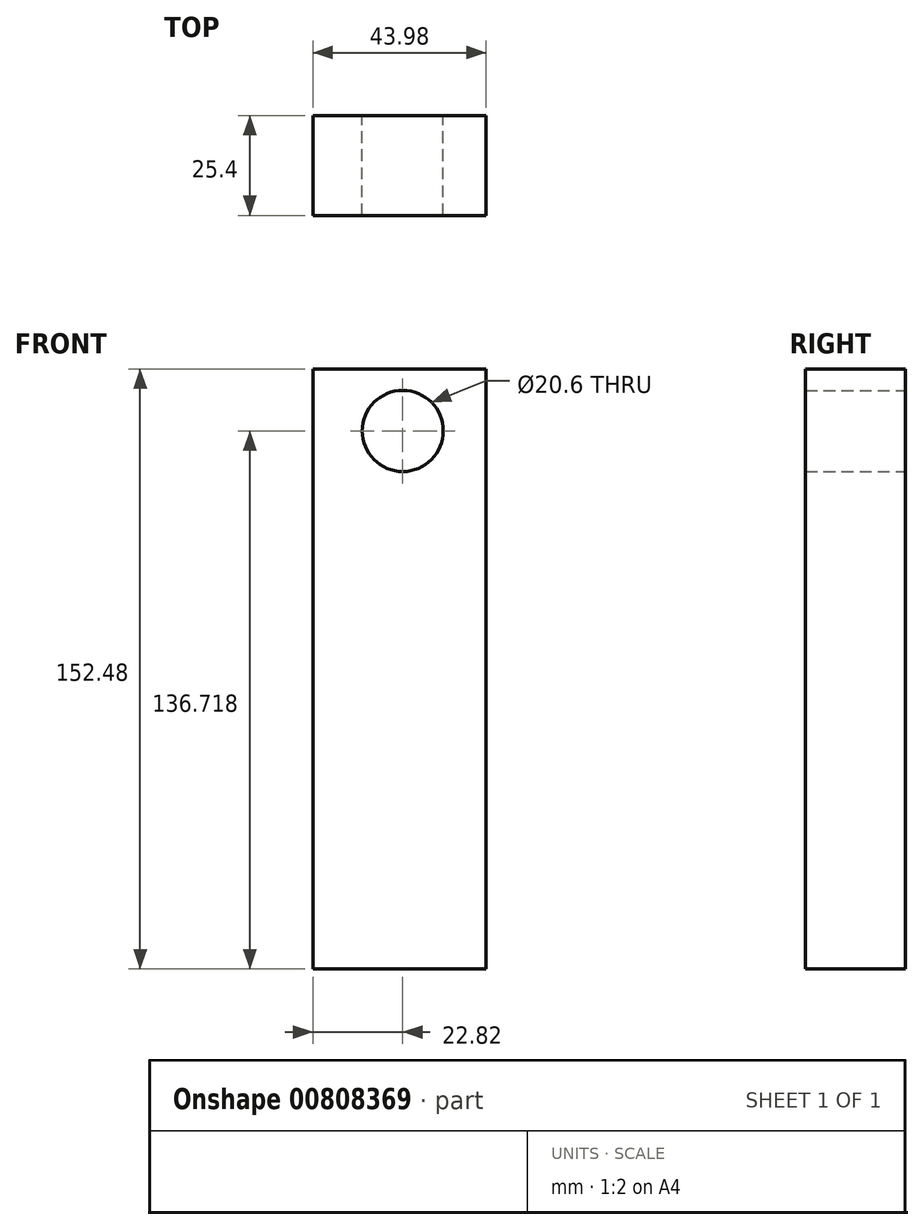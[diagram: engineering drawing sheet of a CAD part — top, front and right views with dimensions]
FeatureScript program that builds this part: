
annotation { "Feature Type Name" : "Feature", "Feature Type Description" : "" }
export const myFeature = defineFeature(function(context is Context, id is Id, definition is map)
    precondition{}
    {
        {
            var Q0;
            Q0=qCreatedBy(makeId("Front.planeOp"),FACE);
            var sketch = newSketch(context, id + "F0", { "sketchPlane" : qUnion([Q0])});
            skLineSegment(sketch, "E0.bottom", {"start": v(-22.82, 75.51) * mm, "end": v(21.16, 75.51) * mm});
            skLineSegment(sketch, "E0.top", {"start": v(-22.82, -76.97) * mm, "end": v(21.16, -76.97) * mm});
            skLineSegment(sketch, "E0.left", {"start": v(-22.82, 75.51) * mm, "end": v(-22.82, -76.97) * mm});
            skLineSegment(sketch, "E0.right", {"start": v(21.16, 75.51) * mm, "end": v(21.16, -76.97) * mm});
            skCircle(sketch, "E1", {"center": v(0, 59.75) * mm, "radius": 10.3 * mm});
            skSolve(sketch);
        }
        {
            var Q0;
            Q0 = qSketchRegion(id + "F0", true);
            extrude(context, id + "F1", {"entities" : qUnion([Q0]), "depth" : 25.4 * mm, "offsetDistance" : 25.4 * mm});
        }
    });
